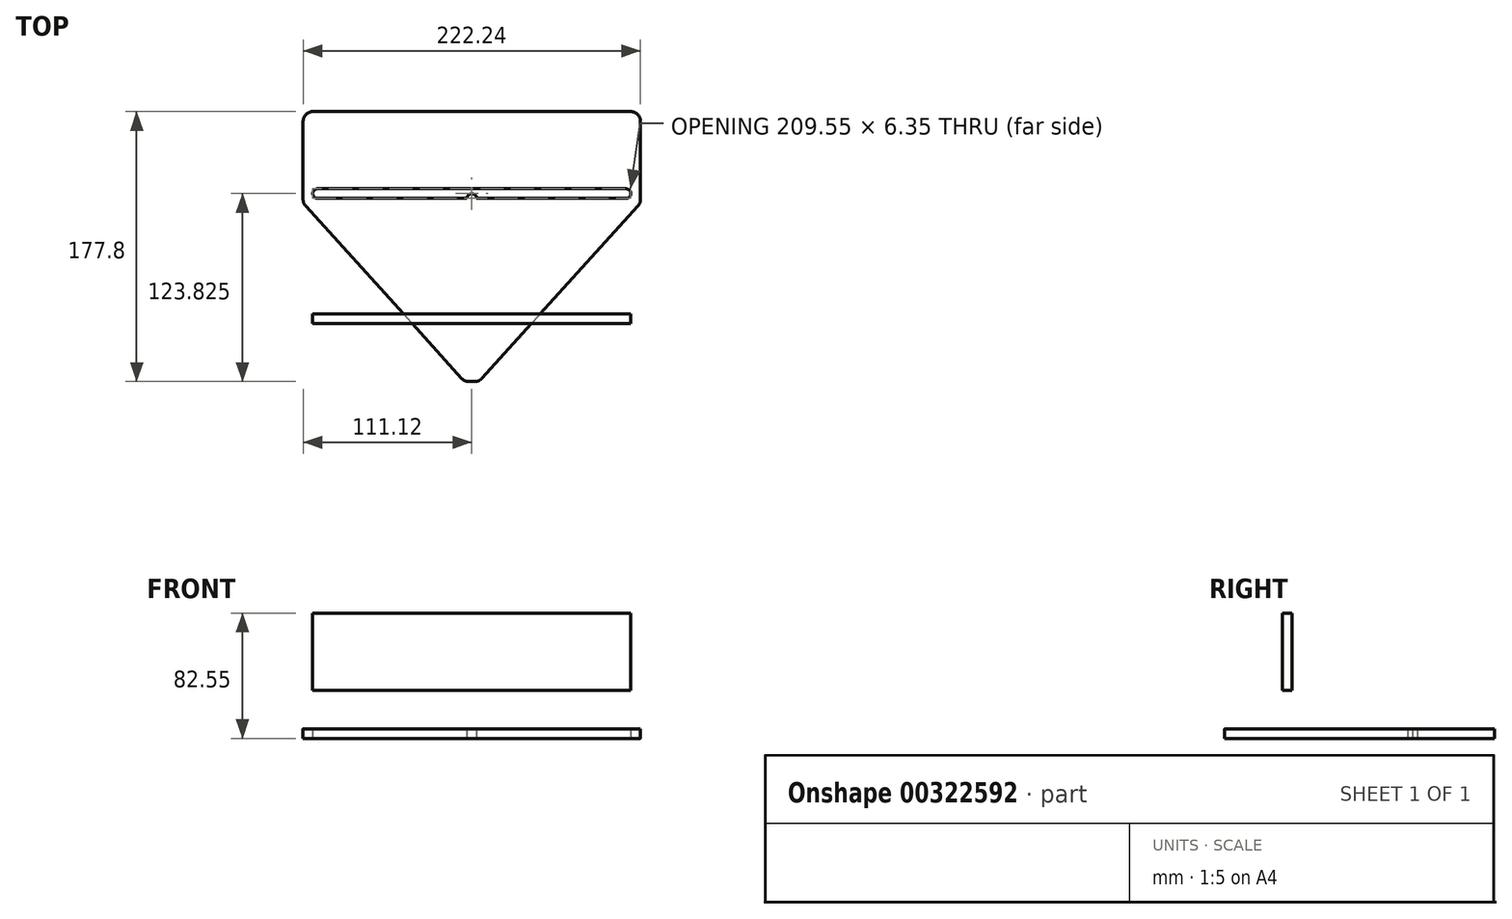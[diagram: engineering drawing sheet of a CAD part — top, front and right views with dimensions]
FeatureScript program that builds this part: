
annotation { "Feature Type Name" : "Feature", "Feature Type Description" : "" }
export const myFeature = defineFeature(function(context is Context, id is Id, definition is map)
    precondition{}
    {
        {
            var Q0;
            Q0=qCreatedBy(makeId("Top.planeOp"),FACE);
            var sketch = newSketch(context, id + "F0", { "sketchPlane" : qUnion([Q0])});
            skLineSegment(sketch, "E0", {"start": v(-111.13, -177.8) * mm, "end": v(111.13, -177.8) * mm});
            skLineSegment(sketch, "E1", {"start": v(111.13, 0) * mm, "end": v(-111.12, 0) * mm});
            skLineSegment(sketch, "E2", {"start": v(0, -177.8) * mm, "end": v(0, 0) * mm, "construction": true});
            skLineSegment(sketch, "E3", {"start": v(-111.13, -177.8) * mm, "end": v(-111.13, 0) * mm});
            skLineSegment(sketch, "E4", {"start": v(111.13, -177.8) * mm, "end": v(111.13, 0) * mm});
            skLineSegment(sketch, "E5", {"start": v(-101.6, -53.98) * mm, "end": v(101.6, -53.98) * mm, "construction": true});
            skArc(sketch, "E6.0.startCap", {"start": v(-101.6, -57.15) * mm, "mid": v(-104.78, -53.98) * mm, "end": v(-101.6, -50.8) * mm});
            skArc(sketch, "E6.0.endCap", {"start": v(101.6, -50.8) * mm, "mid": v(104.78, -53.98) * mm, "end": v(101.6, -57.15) * mm});
            skLineSegment(sketch, "E6.0.left", {"start": v(-101.6, -50.8) * mm, "end": v(101.6, -50.8) * mm});
            skLineSegment(sketch, "E6.0.right", {"start": v(-101.6, -57.15) * mm, "end": v(-3.17, -57.15) * mm});
            skLineSegment(sketch, "E7", {"start": v(0, -57.15) * mm, "end": v(0, -165.1) * mm, "construction": true});
            skArc(sketch, "E8.0.startCap", {"start": v(-3.18, -57.15) * mm, "mid": v(0, -53.98) * mm, "end": v(3.18, -57.15) * mm});
            skArc(sketch, "E8.0.endCap", {"start": v(3.17, -165.1) * mm, "mid": v(0, -168.28) * mm, "end": v(-3.17, -165.1) * mm});
            skLineSegment(sketch, "E8.0.left", {"start": v(3.18, -57.15) * mm, "end": v(3.17, -165.1) * mm});
            skLineSegment(sketch, "E8.0.right", {"start": v(-3.18, -57.15) * mm, "end": v(-3.17, -165.1) * mm});
            skArc(sketch, "E9", {"start": v(-9.53, -57.15) * mm, "mid": v(-6.35, -53.97) * mm, "end": v(-9.53, -50.8) * mm});
            skArc(sketch, "E10", {"start": v(9.53, -50.8) * mm, "mid": v(6.35, -53.97) * mm, "end": v(9.53, -57.15) * mm});
            skLineSegment(sketch, "E11.trimOffspring", {"start": v(3.17, -57.15) * mm, "end": v(101.6, -57.15) * mm});
            skLineSegment(sketch, "E12", {"start": v(-111.13, -60.33) * mm, "end": v(-4.76, -177.8) * mm});
            skLineSegment(sketch, "E13", {"start": v(4.76, -177.8) * mm, "end": v(111.13, -60.32) * mm});
            skSolve(sketch);
        }
        {
            var Q0;
            {var subQ0=sQuery(id+"F0.wireOp",EDGE,"E8.0.startCap");Q0=makeQuery(id+"F0.imprint","IMPRINT",FACE,{"disambiguationData":[TD([[makeQuery(id+"F0.imprint","IMPRINT",EDGE,{"derivedFrom":subQ0}),1.0]])]});}
            var Q1;
            {var subQ12=sQuery(id+"F0.wireOp",EDGE,"E1");Q1=makeQuery(id+"F0.imprint","IMPRINT",FACE,{"disambiguationData":[TD([[makeQuery(id+"F0.imprint","IMPRINT",EDGE,{"derivedFrom":subQ12}),1.0]])]});}
            extrude(context, id + "F1", {"entities" : qUnion([Q0, Q1]), "depth" : 6.35 * mm, "offsetDistance" : 25.4 * mm});
        }
        {
            var Q0;
            Q0=makeQuery(id+"F1.opExtrude","SWEPT_FACE",FACE,{"disambiguationData":[OSD([sQuery(id+"F0.wireOp",EDGE,"E0")])]});
            cPlane(context, id + "F2", {"entities" : qUnion([Q0]), "cplaneType" : CPlaneType.OFFSET, "offset" : 38.1 * mm, "oppositeDirection" : true, "width" : 152.4 * mm, "height" : 152.4 * mm});
        }
        {
            var Q0;
            Q0=qCreatedBy(id+"F2.planeOp",FACE);
            var sketch = newSketch(context, id + "F3", { "sketchPlane" : qUnion([Q0])});
            skLineSegment(sketch, "E14.bottom", {"start": v(-104.77, 82.55) * mm, "end": v(104.77, 82.55) * mm});
            skLineSegment(sketch, "E14.top", {"start": v(-104.77, 31.75) * mm, "end": v(104.77, 31.75) * mm});
            skLineSegment(sketch, "E14.left", {"start": v(-104.77, 82.55) * mm, "end": v(-104.77, 31.75) * mm});
            skLineSegment(sketch, "E14.right", {"start": v(104.77, 82.55) * mm, "end": v(104.77, 31.75) * mm});
            skLineSegment(sketch, "E15.bottom", {"start": v(-104.77, 31.75) * mm, "end": v(-63.5, 31.75) * mm});
            skLineSegment(sketch, "E15.top", {"start": v(-104.77, 6.35) * mm, "end": v(-63.5, 6.35) * mm});
            skLineSegment(sketch, "E15.left", {"start": v(-104.77, 31.75) * mm, "end": v(-104.77, 6.35) * mm});
            skLineSegment(sketch, "E15.right", {"start": v(-63.5, 31.75) * mm, "end": v(-63.5, 6.35) * mm});
            skLineSegment(sketch, "E16.bottom", {"start": v(104.77, 31.75) * mm, "end": v(63.5, 31.75) * mm});
            skLineSegment(sketch, "E16.top", {"start": v(104.77, 6.35) * mm, "end": v(63.5, 6.35) * mm});
            skLineSegment(sketch, "E16.left", {"start": v(104.77, 31.75) * mm, "end": v(104.77, 6.35) * mm});
            skLineSegment(sketch, "E16.right", {"start": v(63.5, 31.75) * mm, "end": v(63.5, 6.35) * mm});
            skLineSegment(sketch, "E17", {"start": v(0, 6.35) * mm, "end": v(0, 82.55) * mm, "construction": true});
            skSolve(sketch);
        }
        {
            var Q0;
            Q0=makeQuery(id+"F3.imprint","IMPRINT",FACE,{"disambiguationData":[TD([[makeQuery(id+"F3.imprint","IMPRINT",EDGE,{"derivedFrom":sQuery(id+"F3.wireOp",EDGE,"E14.bottom")}),-1.0]])]});
            var Q1;
            Q1=makeQuery(id+"F3.imprint","IMPRINT",FACE,{"disambiguationData":[TD([[makeQuery(id+"F3.imprint","IMPRINT",EDGE,{"derivedFrom":sQuery(id+"F3.wireOp",EDGE,"E15.bottom")}),-1.0]])]});
            var Q2;
            Q2=makeQuery(id+"F3.imprint","IMPRINT",FACE,{"disambiguationData":[TD([[makeQuery(id+"F3.imprint","IMPRINT",EDGE,{"derivedFrom":sQuery(id+"F3.wireOp",EDGE,"E16.bottom")}),1.0]])]});
            extrude(context, id + "F4", {"entities" : qUnion([Q0, Q1, Q2]), "oppositeDirection" : true, "depth" : 6.35 * mm, "offsetDistance" : 25.4 * mm});
        }
        {
            var Q0;
            Q0=makeQuery(id+"F1.opExtrude","SWEPT_EDGE",EDGE,{"disambiguationData":[OSD([sQuery(id+"F0.wireOp",EDGE,"E3"),sQuery(id+"F0.wireOp",EDGE,"E12")])]});
            var Q1;
            Q1=makeQuery(id+"F1.opExtrude","SWEPT_EDGE",EDGE,{"disambiguationData":[OSD([sQuery(id+"F0.wireOp",EDGE,"E1"),sQuery(id+"F0.wireOp",EDGE,"E3")])]});
            var Q2;
            Q2=makeQuery(id+"F1.opExtrude","SWEPT_EDGE",EDGE,{"disambiguationData":[OSD([sQuery(id+"F0.wireOp",EDGE,"E0"),sQuery(id+"F0.wireOp",EDGE,"E12")])]});
            var Q3;
            Q3=makeQuery(id+"F1.opExtrude","SWEPT_EDGE",EDGE,{"disambiguationData":[OSD([sQuery(id+"F0.wireOp",EDGE,"E0"),sQuery(id+"F0.wireOp",EDGE,"E13")])]});
            var Q4;
            Q4=makeQuery(id+"F1.opExtrude","SWEPT_EDGE",EDGE,{"disambiguationData":[OSD([sQuery(id+"F0.wireOp",EDGE,"E1"),sQuery(id+"F0.wireOp",EDGE,"E4")])]});
            var Q5;
            Q5=makeQuery(id+"F1.opExtrude","SWEPT_EDGE",EDGE,{"disambiguationData":[OSD([sQuery(id+"F0.wireOp",EDGE,"E4"),sQuery(id+"F0.wireOp",EDGE,"E13")])]});
            fillet(context, id + "F5", {"entities" : qUnion([Q0, Q1, Q2, Q3, Q4, Q5]), "radius" : 6.35 * mm, "tangentPropagation" : true, "allowEdgeOverflow" : false});
        }
    });
